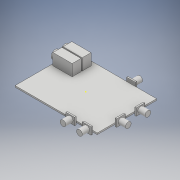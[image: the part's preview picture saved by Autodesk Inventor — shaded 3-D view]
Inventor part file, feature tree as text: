
AUTODESK INVENTOR PART (.ipt)
format: ipt  version: 2018 (Build 220112000, 112)  size: 223,744 bytes
history: native  units: mm
features: sketch x11, extrude x9
ambient origin geometry x8: Origin, YZ Plane, XZ Plane, XY Plane, X Axis, Y Axis, Z Axis, Center Point
bodies: Solid1 (feature_tree)
feature tree (20):
  extrude  "Extrusion1"  Depth=65.0mm
  sketch  "Sketch2"  dims[d2=1.6mm d3=0.0mm d4=9.55mm]
  sketch  "Sketch3"  dims[d5=8.0mm d6=1.55mm d7=0.0mm]
  extrude  "Extrusion2"  Depth=9.55mm
  extrude  "Extrusion3"  Depth=1.55mm TaperAngle=0.0deg
  extrude  "Extrusion4"  Depth=9.55mm
  extrude  "Extrusion5"  Depth=8.0mm
  extrude  "Extrusion6"  Depth=1.55mm TaperAngle=0.0deg
  extrude  "Extrusion7"  Depth=10.0mm
  extrude  "Extrusion8"  Depth=9.55mm
  extrude  "Extrusion9"  Depth=21.0mm
  sketch  "Sketch1"  dims[d0=90.0mm d1=65.0mm]
  sketch  "Sketch4"  dims[d8=62.0mm d9=9.55mm]
  sketch  "Sketch5"  dims[d10=8.0mm d11=19.0mm]
  sketch  "Sketch6"  dims[d12=24.5mm d13=1.55mm d14=0.0mm]
  sketch  "Sketch7"  dims[d15=10.0mm d16=28.0mm]
  sketch  "Sketch8"  dims[d17=8.0mm d18=9.55mm]
  sketch  "Sketch9"  dims[d19=1.55mm d20=0.0mm d21=21.0mm]
  sketch  "Sketch10"  dims[d22=9.75mm]
  sketch  "Sketch11"  dims[d23=25.5mm d24=4.8mm d25=2.0mm d26=12.6mm d27=0.0mm d28=9.0mm d29=2.4mm d30=0.0mm d31=6.25mm d32=8.0mm d33=0.0mm d34=6.25mm d35=8.0mm d36=0.0mm d37=6.25mm d38=8.0mm d39=0.0mm]
